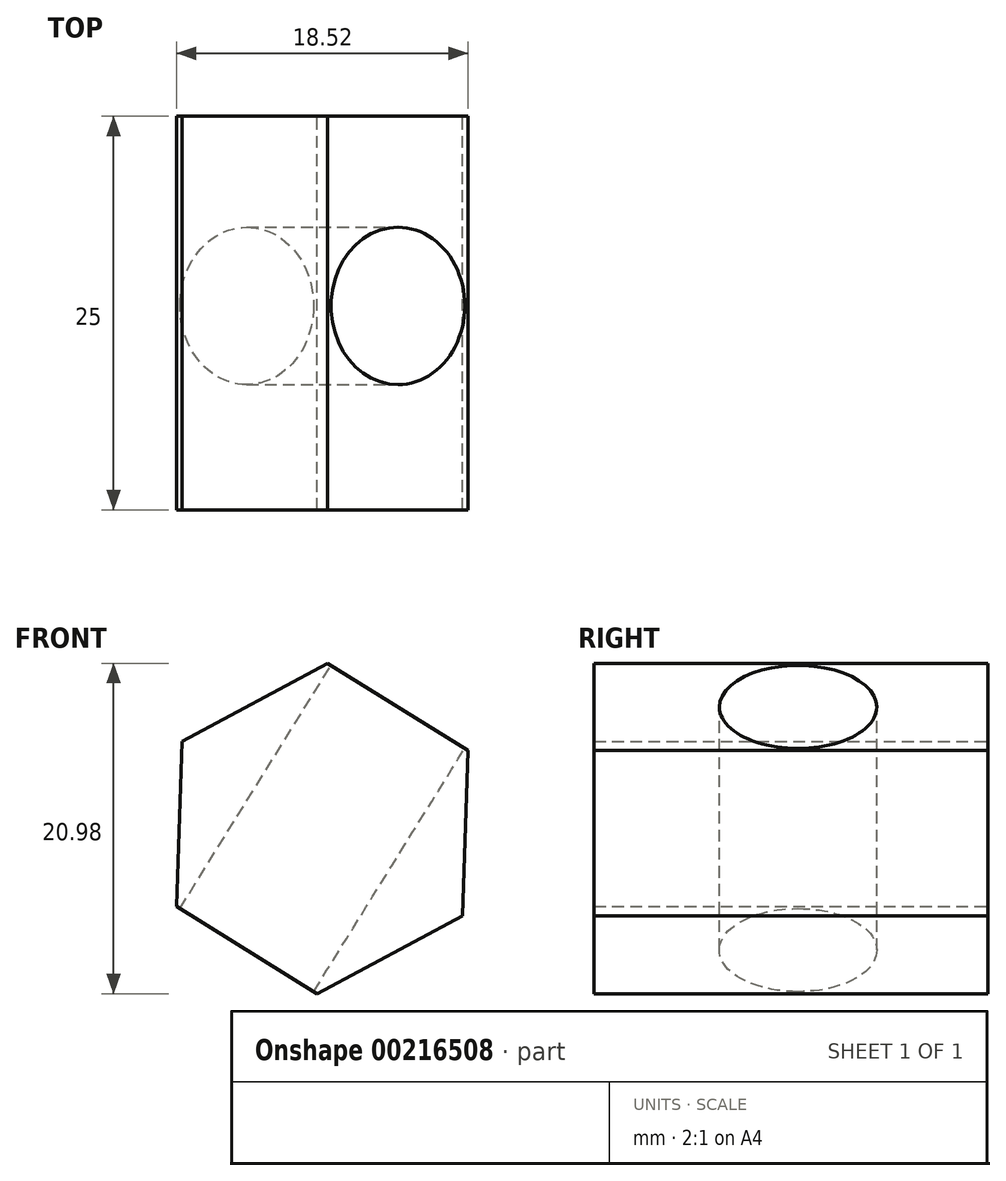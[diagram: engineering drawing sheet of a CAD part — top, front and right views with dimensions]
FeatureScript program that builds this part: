
annotation { "Feature Type Name" : "Feature", "Feature Type Description" : "" }
export const myFeature = defineFeature(function(context is Context, id is Id, definition is map)
    precondition{}
    {
        {
            var Q0;
            Q0=qCreatedBy(makeId("Front.planeOp"),FACE);
            var sketch = newSketch(context, id + "F0", { "sketchPlane" : qUnion([Q0])});
            skCircle(sketch, "E0.cCircle", {"center": v(0, 0) * mm, "radius": 10.5 * mm, "construction": true});
            skLineSegment(sketch, "E0.0", {"start": v(9.26, 4.95) * mm, "end": v(8.92, -5.54) * mm});
            skLineSegment(sketch, "E0.1", {"start": v(8.92, -5.54) * mm, "end": v(-0.34, -10.5) * mm});
            skLineSegment(sketch, "E0.2", {"start": v(-0.34, -10.5) * mm, "end": v(-9.26, -4.95) * mm});
            skLineSegment(sketch, "E0.3", {"start": v(-9.26, -4.95) * mm, "end": v(-8.92, 5.54) * mm});
            skLineSegment(sketch, "E0.4", {"start": v(-8.92, 5.54) * mm, "end": v(0.34, 10.5) * mm});
            skLineSegment(sketch, "E0.5", {"start": v(0.34, 10.5) * mm, "end": v(9.26, 4.95) * mm});
            skSolve(sketch);
        }
        {
            var Q0;
            Q0=makeQuery(id+"F0.imprint","IMPRINT",FACE,{"disambiguationData":[TD([[makeQuery(id+"F0.imprint","IMPRINT",EDGE,{"derivedFrom":sQuery(id+"F0.wireOp",EDGE,"E0.0")}),-1.0]])]});
            extrude(context, id + "F1", {"entities" : qUnion([Q0]), "depth" : 25 * mm});
        }
        {
            var Q0;
            Q0=makeQuery(id+"F1.opExtrude","SWEPT_FACE",FACE,{"disambiguationData":[OSD([sQuery(id+"F0.wireOp",EDGE,"E0.5")])]});
            var sketch = newSketch(context, id + "F2", { "sketchPlane" : qUnion([Q0])});
            skPoint(sketch, "E1", {"position": v(0, -12.04) * mm});
            skSolve(sketch);
        }
        {
            var Q0;
            Q0=sQuery(id+"F2.wireOp",VERTEX,"E1");
            var Q1;
            Q1=makeQuery(id+"F1.opExtrude","SWEPT_BODY",BODY,{"disambiguationData":[OSD([sQuery(id+"F0.wireOp",EDGE,"E0.0"),sQuery(id+"F0.wireOp",EDGE,"E0.1"),sQuery(id+"F0.wireOp",EDGE,"E0.2"),sQuery(id+"F0.wireOp",EDGE,"E0.3"),sQuery(id+"F0.wireOp",EDGE,"E0.4"),sQuery(id+"F0.wireOp",EDGE,"E0.5")])]});
            hole(context, id + "F3", {"style" : HoleStyle.SIMPLE, "endStyle" : HoleEndStyle.THROUGH, "holeDiameter" : 10 * mm, "tappedDepth" : 12 * mm, "tapClearance" : 3, "startFromSketch" : true, "locations" : qUnion([Q0]), "scope" : qUnion([Q1])});
        }
    });
